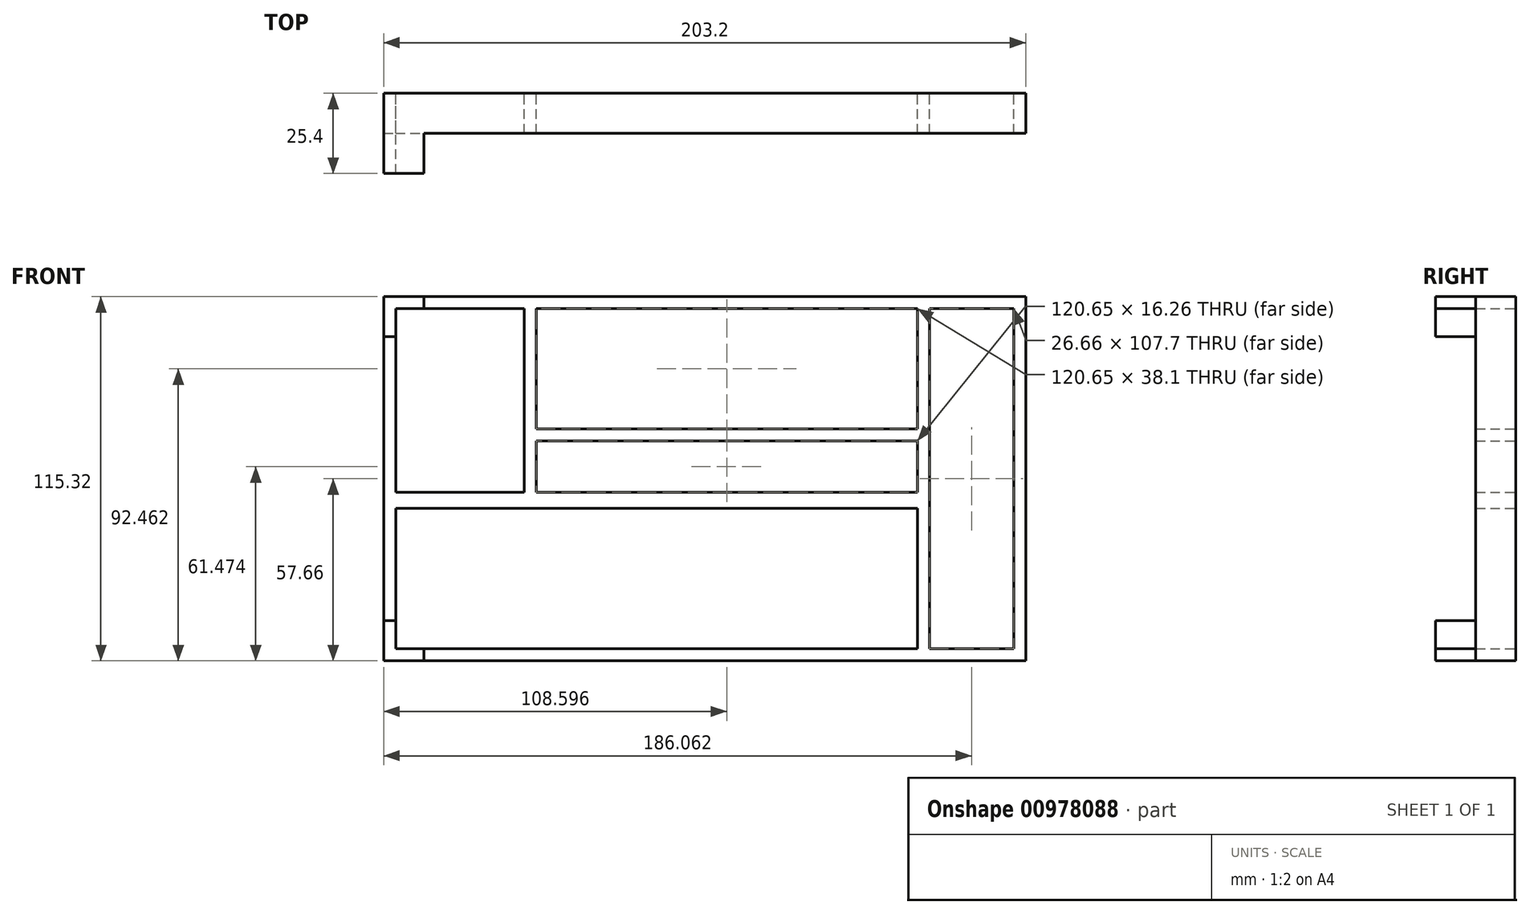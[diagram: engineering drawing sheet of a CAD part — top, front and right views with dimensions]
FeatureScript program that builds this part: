
annotation { "Feature Type Name" : "Feature", "Feature Type Description" : "" }
export const myFeature = defineFeature(function(context is Context, id is Id, definition is map)
    precondition{}
    {
        {
            var Q0;
            Q0=qCreatedBy(makeId("Front.planeOp"),FACE);
            var sketch = newSketch(context, id + "F0", { "sketchPlane" : qUnion([Q0])});
            skLineSegment(sketch, "E0.top", {"start": v(-81.04, -48) * mm, "end": v(84.07, -48) * mm});
            skLineSegment(sketch, "E0.left", {"start": v(-81.04, -3.56) * mm, "end": v(-81.04, -48) * mm});
            skLineSegment(sketch, "E1.top", {"start": v(-84.85, -51.82) * mm, "end": v(118.35, -51.82) * mm});
            skLineSegment(sketch, "E2.top", {"start": v(118.35, 63.5) * mm, "end": v(-84.85, 63.5) * mm});
            skLineSegment(sketch, "E3.left", {"start": v(-81.04, 1.52) * mm, "end": v(-81.04, 59.7) * mm});
            skLineSegment(sketch, "E3.right", {"start": v(84.07, 21.6) * mm, "end": v(84.07, 59.7) * mm});
            skPoint(sketch, "E4.endSnap0", {"position": v(1.51, 21.6) * mm});
            skLineSegment(sketch, "E5.left", {"start": v(-40.39, 59.7) * mm, "end": v(-40.39, 1.52) * mm});
            skLineSegment(sketch, "E5.right", {"start": v(-36.58, 59.7) * mm, "end": v(-36.58, 21.6) * mm});
            skLineSegment(sketch, "E6", {"start": v(-84.85, 63.5) * mm, "end": v(-84.85, -51.82) * mm});
            skLineSegment(sketch, "E7", {"start": v(-81.04, 1.52) * mm, "end": v(-40.39, 1.52) * mm});
            skLineSegment(sketch, "E8", {"start": v(-81.04, 59.7) * mm, "end": v(-40.39, 59.7) * mm});
            skLineSegment(sketch, "E9", {"start": v(-36.58, 59.7) * mm, "end": v(84.07, 59.7) * mm});
            skLineSegment(sketch, "E10", {"start": v(84.07, 21.6) * mm, "end": v(-36.58, 21.6) * mm});
            skLineSegment(sketch, "E11", {"start": v(-36.58, 17.78) * mm, "end": v(84.07, 17.78) * mm});
            skLineSegment(sketch, "E12", {"start": v(118.35, -51.82) * mm, "end": v(118.35, 63.5) * mm});
            skLineSegment(sketch, "E13.bottom", {"start": v(87.88, 59.7) * mm, "end": v(114.54, 59.7) * mm});
            skLineSegment(sketch, "E13.top", {"start": v(87.88, -48.01) * mm, "end": v(114.54, -48.01) * mm});
            skLineSegment(sketch, "E13.left", {"start": v(87.88, 59.7) * mm, "end": v(87.88, -48.01) * mm});
            skLineSegment(sketch, "E13.right", {"start": v(114.54, 59.7) * mm, "end": v(114.54, -48.01) * mm});
            skLineSegment(sketch, "E14", {"start": v(84.07, 17.78) * mm, "end": v(84.07, -48) * mm});
            skLineSegment(sketch, "E15", {"start": v(-36.58, 17.78) * mm, "end": v(-36.58, 1.52) * mm});
            skLineSegment(sketch, "E16", {"start": v(-36.58, 1.52) * mm, "end": v(84.07, 1.52) * mm});
            skLineSegment(sketch, "E17", {"start": v(-81.04, -3.56) * mm, "end": v(84.07, -3.56) * mm});
            skPoint(sketch, "E17.endSnap0", {"position": v(84.07, -15.11) * mm});
            skSolve(sketch);
        }
        {
            var Q0;
            Q0=makeQuery(id+"F0.imprint","IMPRINT",FACE,{"disambiguationData":[TD([[makeQuery(id+"F0.imprint","IMPRINT",EDGE,{"derivedFrom":sQuery(id+"F0.wireOp",EDGE,"E0.top")}),-1.0]])]});
            extrude(context, id + "F1", {"entities" : qUnion([Q0]), "depth" : 12.7 * mm, "offsetDistance" : 25.4 * mm});
        }
        {
            var Q0;
            Q0=makeQuery(id+"F1.opExtrude","CAP_FACE",FACE,{"disambiguationData":[OSD([sQuery(id+"F0.wireOp",EDGE,"E0.top"),sQuery(id+"F0.wireOp",EDGE,"E0.left"),sQuery(id+"F0.wireOp",EDGE,"E1.top"),sQuery(id+"F0.wireOp",EDGE,"E2.top"),sQuery(id+"F0.wireOp",EDGE,"E3.left"),sQuery(id+"F0.wireOp",EDGE,"E3.right"),sQuery(id+"F0.wireOp",EDGE,"E5.left"),sQuery(id+"F0.wireOp",EDGE,"E5.right"),sQuery(id+"F0.wireOp",EDGE,"E6"),sQuery(id+"F0.wireOp",EDGE,"E7"),sQuery(id+"F0.wireOp",EDGE,"E8"),sQuery(id+"F0.wireOp",EDGE,"E9"),sQuery(id+"F0.wireOp",EDGE,"E10"),sQuery(id+"F0.wireOp",EDGE,"E11"),sQuery(id+"F0.wireOp",EDGE,"E12"),sQuery(id+"F0.wireOp",EDGE,"E13.bottom"),sQuery(id+"F0.wireOp",EDGE,"E13.top"),sQuery(id+"F0.wireOp",EDGE,"E13.left"),sQuery(id+"F0.wireOp",EDGE,"E13.right"),sQuery(id+"F0.wireOp",EDGE,"E14"),sQuery(id+"F0.wireOp",EDGE,"E15"),sQuery(id+"F0.wireOp",EDGE,"E16"),sQuery(id+"F0.wireOp",EDGE,"E17")])],"isStart":false});
            var sketch = newSketch(context, id + "F2", { "sketchPlane" : qUnion([Q0])});
            skLineSegment(sketch, "E18.bottom", {"start": v(-84.85, 63.5) * mm, "end": v(-72.15, 63.5) * mm});
            skLineSegment(sketch, "E18.top", {"start": v(-84.85, 59.7) * mm, "end": v(-72.15, 59.7) * mm});
            skLineSegment(sketch, "E18.left", {"start": v(-84.85, 63.5) * mm, "end": v(-84.85, 59.7) * mm});
            skLineSegment(sketch, "E18.right", {"start": v(-72.15, 63.5) * mm, "end": v(-72.15, 59.7) * mm});
            skLineSegment(sketch, "E19.bottom", {"start": v(-84.85, 59.7) * mm, "end": v(-81.04, 59.7) * mm});
            skLineSegment(sketch, "E19.top", {"start": v(-84.85, 50.8) * mm, "end": v(-81.04, 50.8) * mm});
            skLineSegment(sketch, "E19.left", {"start": v(-84.85, 59.7) * mm, "end": v(-84.85, 50.8) * mm});
            skLineSegment(sketch, "E19.right", {"start": v(-81.04, 59.7) * mm, "end": v(-81.04, 50.8) * mm});
            skLineSegment(sketch, "E20.bottom", {"start": v(-84.85, -51.82) * mm, "end": v(-81.04, -51.82) * mm});
            skLineSegment(sketch, "E20.top", {"start": v(-84.85, -39.12) * mm, "end": v(-81.04, -39.12) * mm});
            skLineSegment(sketch, "E20.left", {"start": v(-84.85, -51.82) * mm, "end": v(-84.85, -39.12) * mm});
            skLineSegment(sketch, "E20.right", {"start": v(-81.04, -51.82) * mm, "end": v(-81.04, -39.12) * mm});
            skLineSegment(sketch, "E21.bottom", {"start": v(-81.04, -51.82) * mm, "end": v(-72.15, -51.82) * mm});
            skLineSegment(sketch, "E21.top", {"start": v(-81.04, -48) * mm, "end": v(-72.15, -48) * mm});
            skLineSegment(sketch, "E21.left", {"start": v(-81.04, -51.82) * mm, "end": v(-81.04, -48) * mm});
            skLineSegment(sketch, "E21.right", {"start": v(-72.15, -51.82) * mm, "end": v(-72.15, -48) * mm});
            skSolve(sketch);
        }
        {
            var Q0;
            Q0=makeQuery(id+"F2.imprint","IMPRINT",FACE,{"disambiguationData":[TD([[makeQuery(id+"F2.imprint","IMPRINT",EDGE,{"derivedFrom":sQuery(id+"F2.wireOp",EDGE,"E19.top")}),1.0]])]});
            var Q1;
            Q1=makeQuery(id+"F2.imprint","IMPRINT",FACE,{"disambiguationData":[TD([[makeQuery(id+"F2.imprint","IMPRINT",EDGE,{"derivedFrom":sQuery(id+"F2.wireOp",EDGE,"E18.bottom")}),1.0]])]});
            var Q2;
            {var subQ2=sQuery(id+"F2.wireOp",EDGE,"E20.bottom");Q2=makeQuery(id+"F2.imprint","IMPRINT",FACE,{"disambiguationData":[TD([[makeQuery(id+"F2.imprint","IMPRINT",EDGE,{"derivedFrom":subQ2}),1.0]])]});}
            var Q3;
            {var subQ2=sQuery(id+"F2.wireOp",EDGE,"E21.bottom");Q3=makeQuery(id+"F2.imprint","IMPRINT",FACE,{"disambiguationData":[TD([[makeQuery(id+"F2.imprint","IMPRINT",EDGE,{"derivedFrom":subQ2}),1.0]])]});}
            extrude(context, id + "F3", {"entities" : qUnion([Q0, Q1, Q2, Q3]), "operationType" : NewBodyOperationType.ADD, "depth" : 12.7 * mm, "offsetDistance" : 25.4 * mm});
        }
    });
